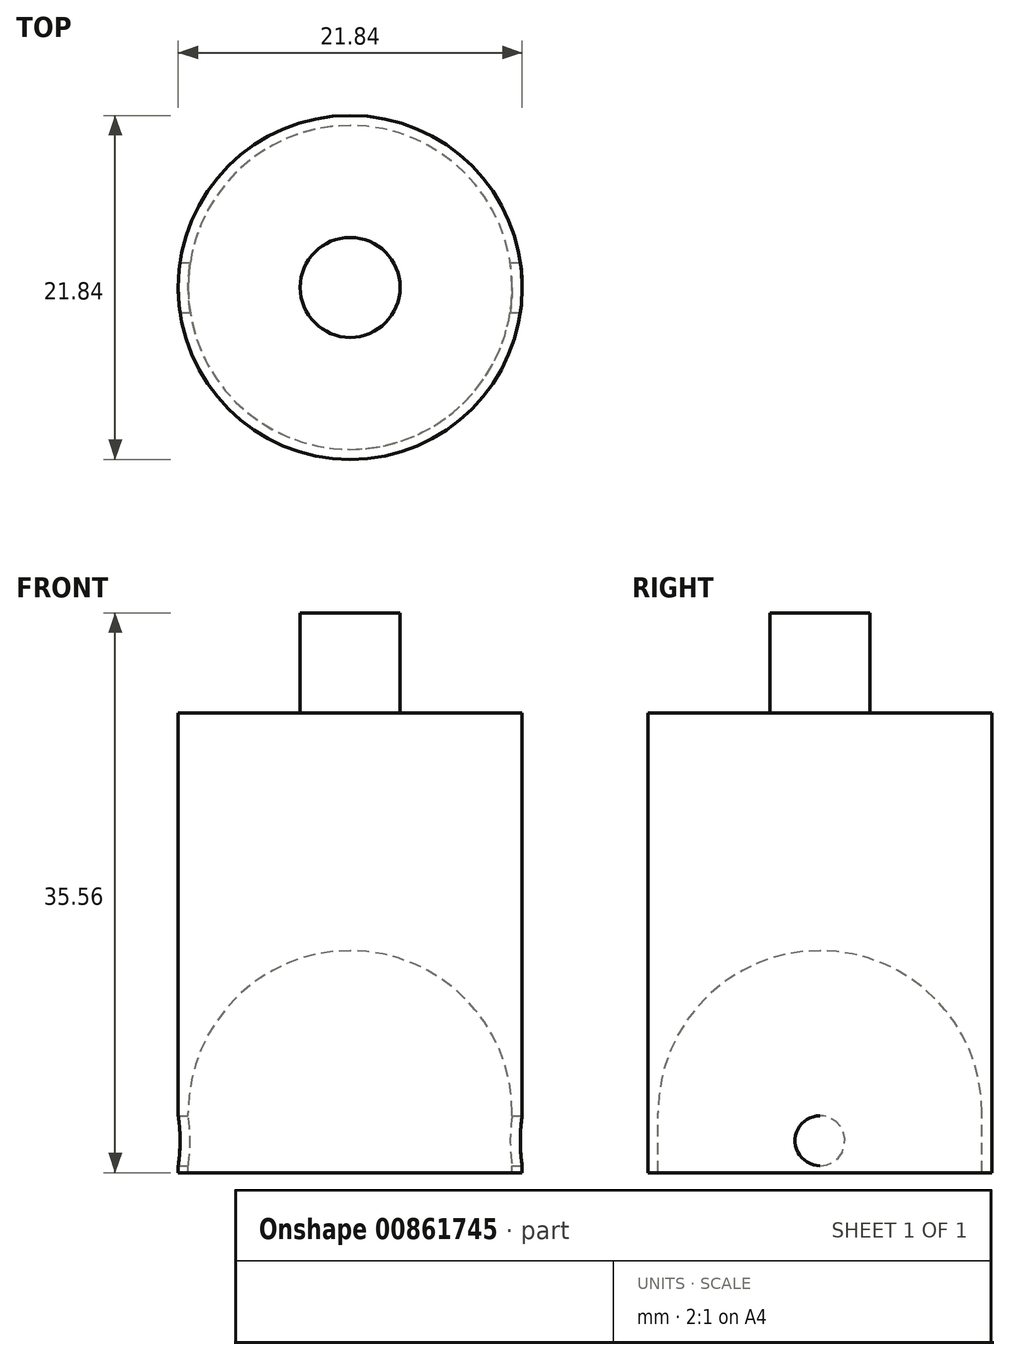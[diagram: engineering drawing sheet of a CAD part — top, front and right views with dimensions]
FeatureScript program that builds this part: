
annotation { "Feature Type Name" : "Feature", "Feature Type Description" : "" }
export const myFeature = defineFeature(function(context is Context, id is Id, definition is map)
    precondition{}
    {
        {
            var Q0;
            Q0=qCreatedBy(makeId("Front.planeOp"),FACE);
            var sketch = newSketch(context, id + "F0", { "sketchPlane" : qUnion([Q0])});
            skLineSegment(sketch, "E0.bottom", {"start": v(10.92, -12.7) * mm, "end": v(0, -12.7) * mm});
            skLineSegment(sketch, "E0.top", {"start": v(10.92, 12.7) * mm, "end": v(0, 12.7) * mm});
            skLineSegment(sketch, "E0.left", {"start": v(10.92, -12.7) * mm, "end": v(10.92, 12.7) * mm});
            skPoint(sketch, "E0.middle", {"position": v(0, 0) * mm});
            skLineSegment(sketch, "E1", {"start": v(0, 12.7) * mm, "end": v(0, -12.7) * mm});
            skPoint(sketch, "E0.right.end.orphan", {"position": v(-10.92, 12.7) * mm});
            skPoint(sketch, "E2.orphan", {"position": v(-10.92, -12.7) * mm});
            skSolve(sketch);
        }
        {
            var Q0;
            Q0=makeQuery(id+"F0.imprint","IMPRINT",FACE,{"disambiguationData":[TD([[makeQuery(id+"F0.imprint","IMPRINT",EDGE,{"derivedFrom":sQuery(id+"F0.wireOp",EDGE,"E0.bottom")}),-1.0]])]});
            var Q1;
            Q1=sQuery(id+"F0.wireOp",EDGE,"E1");
            revolve(context, id + "F1", {"surfaceOperationType" : NewSurfaceOperationType.NEW, "entities" : qUnion([Q0]), "axis" : qUnion([Q1]), "revolveType" : RevolveType.FULL});
        }
        {
            var Q0;
            Q0=makeQuery(id+"F1.opRevolve","SWEPT_FACE",FACE,{"disambiguationData":[OSD([sQuery(id+"F0.wireOp",EDGE,"E0.bottom")])]});
            var sketch = newSketch(context, id + "F2", { "sketchPlane" : qUnion([Q0])});
            skArc(sketch, "E3", {"start": v(0, -10.29) * mm, "mid": v(10.29, 0) * mm, "end": v(0, 10.29) * mm});
            skLineSegment(sketch, "E4", {"start": v(0, 10.29) * mm, "end": v(0, -10.29) * mm});
            skSolve(sketch);
        }
        {
            var Q0;
            Q0=makeQuery(id+"F2.imprint","IMPRINT",FACE,{"disambiguationData":[TD([[makeQuery(id+"F2.imprint","IMPRINT",EDGE,{"derivedFrom":sQuery(id+"F2.wireOp",EDGE,"E3")}),1.0]])]});
            var Q1;
            Q1=sQuery(id+"F2.wireOp",EDGE,"E4");
            revolve(context, id + "F3", {"operationType" : NewBodyOperationType.REMOVE, "surfaceOperationType" : NewSurfaceOperationType.NEW, "entities" : qUnion([Q0]), "axis" : qUnion([Q1]), "revolveType" : RevolveType.FULL, "oppositeDirection" : true});
        }
        {
            var Q0;
            Q0=qCreatedBy(makeId("Front.planeOp"),FACE);
            var sketch = newSketch(context, id + "F4", { "sketchPlane" : qUnion([Q0])});
            skLineSegment(sketch, "E5.bottom", {"start": v(10.92, -12.7) * mm, "end": v(10.29, -12.7) * mm});
            skLineSegment(sketch, "E5.top", {"start": v(10.92, -16.5) * mm, "end": v(10.29, -16.5) * mm});
            skLineSegment(sketch, "E5.left", {"start": v(10.92, -12.7) * mm, "end": v(10.92, -16.5) * mm});
            skLineSegment(sketch, "E5.right", {"start": v(10.29, -12.7) * mm, "end": v(10.29, -16.5) * mm});
            skLineSegment(sketch, "E6", {"start": v(0, 0) * mm, "end": v(0, -12.66) * mm});
            skSolve(sketch);
        }
        {
            var Q0;
            Q0=makeQuery(id+"F4.imprint","IMPRINT",FACE,{"disambiguationData":[TD([[makeQuery(id+"F4.imprint","IMPRINT",EDGE,{"derivedFrom":sQuery(id+"F4.wireOp",EDGE,"E5.bottom")}),1.0]])]});
            var Q1;
            Q1=sQuery(id+"F4.wireOp",EDGE,"E6");
            revolve(context, id + "F5", {"operationType" : NewBodyOperationType.ADD, "surfaceOperationType" : NewSurfaceOperationType.NEW, "entities" : qUnion([Q0]), "axis" : qUnion([Q1]), "revolveType" : RevolveType.FULL});
        }
        {
            var Q0;
            Q0=qCreatedBy(makeId("Right.planeOp"),FACE);
            var sketch = newSketch(context, id + "F6", { "sketchPlane" : qUnion([Q0])});
            skCircle(sketch, "E7", {"center": v(0, -14.48) * mm, "radius": 1.59 * mm});
            skSolve(sketch);
        }
        {
            var Q0;
            Q0 = qSketchRegion(id + "F6", true);
            extrude(context, id + "F7", {"entities" : qUnion([Q0]), "operationType" : NewBodyOperationType.REMOVE, "oppositeDirection" : true, "depth" : 25.4 * mm, "offsetDistance" : 25.4 * mm, "symmetric" : true});
        }
        {
            var Q0;
            Q0=makeQuery(id+"F1.opRevolve","SWEPT_FACE",FACE,{"disambiguationData":[OSD([sQuery(id+"F0.wireOp",EDGE,"E0.top")])]});
            var sketch = newSketch(context, id + "F8", { "sketchPlane" : qUnion([Q0])});
            skCircle(sketch, "E8", {"center": v(0, 0) * mm, "radius": 3.18 * mm});
            skSolve(sketch);
        }
        {
            var Q0;
            Q0 = qSketchRegion(id + "F8", true);
            extrude(context, id + "F9", {"entities" : qUnion([Q0]), "operationType" : NewBodyOperationType.ADD, "depth" : 6.35 * mm, "offsetDistance" : 25.4 * mm});
        }
    });
